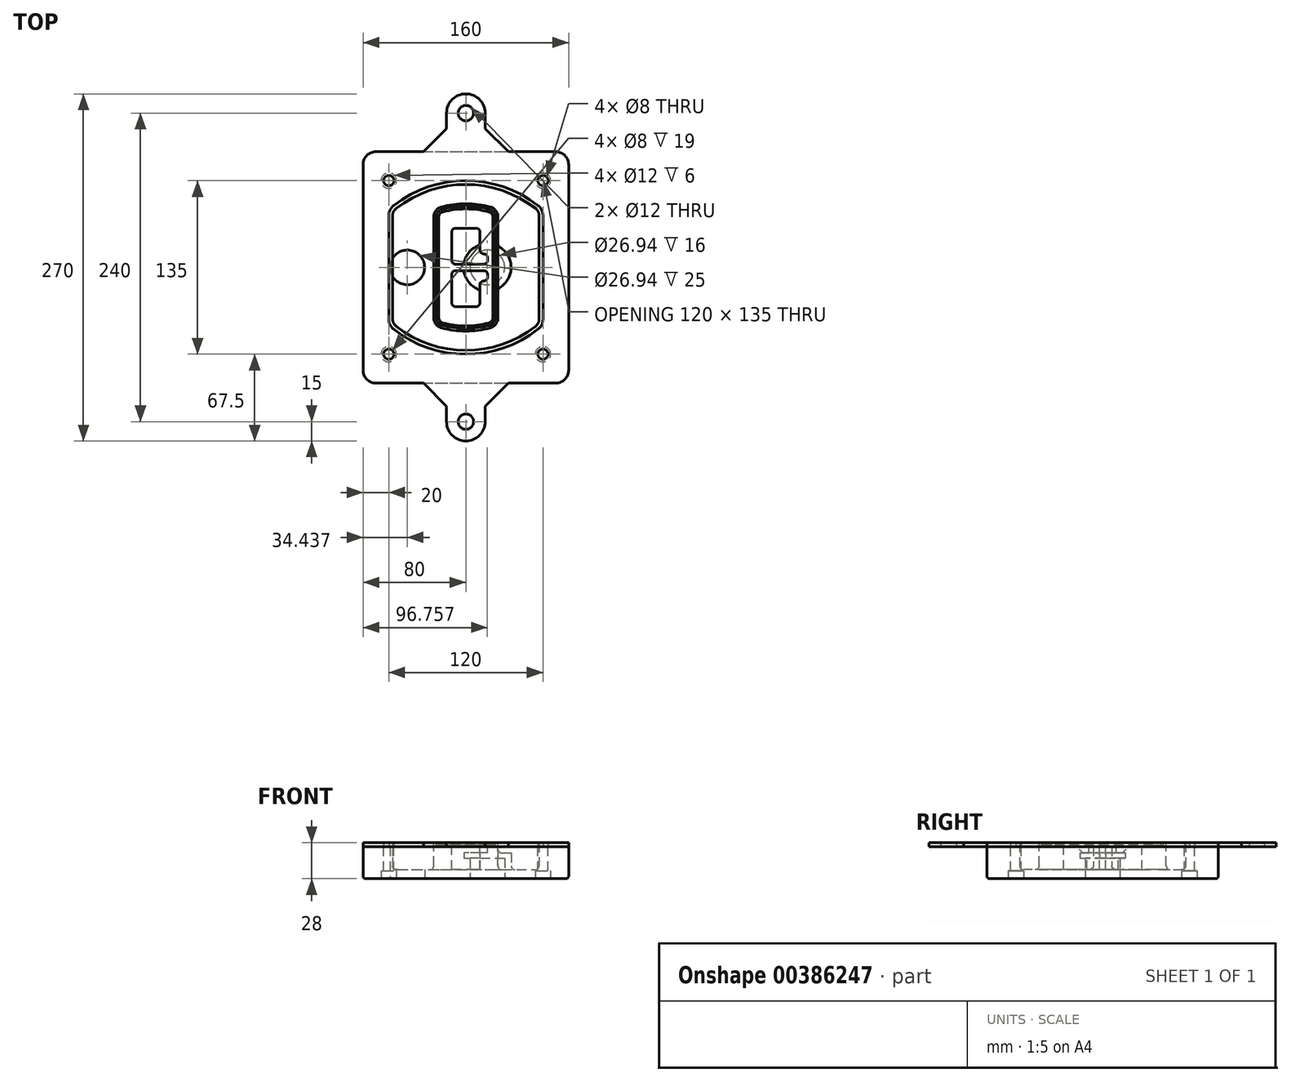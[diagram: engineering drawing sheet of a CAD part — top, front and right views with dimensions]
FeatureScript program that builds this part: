
annotation { "Feature Type Name" : "Feature", "Feature Type Description" : "" }
export const myFeature = defineFeature(function(context is Context, id is Id, definition is map)
    precondition{}
    {
        {
            var Q0;
            Q0=qCreatedBy(makeId("Top.planeOp"),FACE);
            var sketch = newSketch(context, id + "F0", { "sketchPlane" : qUnion([Q0])});
            skPoint(sketch, "E0.rect.middle", {"position": v(0, 0) * mm});
            skLineSegment(sketch, "E1.bottom", {"start": v(-70, -90) * mm, "end": v(70, -90) * mm});
            skLineSegment(sketch, "E1.top", {"start": v(-70, 90) * mm, "end": v(70, 90) * mm});
            skLineSegment(sketch, "E1.left", {"start": v(-80, -80) * mm, "end": v(-80, 80) * mm});
            skLineSegment(sketch, "E1.right", {"start": v(80, -80) * mm, "end": v(80, 80) * mm});
            skLineSegment(sketch, "E2", {"start": v(-80, 90) * mm, "end": v(80, -90) * mm, "construction": true});
            skLineSegment(sketch, "E3", {"start": v(80, 90) * mm, "end": v(-80, -90) * mm, "construction": true});
            skCircle(sketch, "E4", {"center": v(-60, 67.5) * mm, "radius": 4 * mm});
            skCircle(sketch, "E5", {"center": v(60, 67.5) * mm, "radius": 4 * mm});
            skCircle(sketch, "E6", {"center": v(60, -67.5) * mm, "radius": 4 * mm});
            skCircle(sketch, "E7", {"center": v(-60, -67.5) * mm, "radius": 4 * mm});
            skLineSegment(sketch, "E8", {"start": v(-60, 67.5) * mm, "end": v(60, 67.5) * mm, "construction": true});
            skLineSegment(sketch, "E9", {"start": v(60, 67.5) * mm, "end": v(60, -67.5) * mm, "construction": true});
            skLineSegment(sketch, "E10", {"start": v(60, -67.5) * mm, "end": v(-60, -67.5) * mm, "construction": true});
            skLineSegment(sketch, "E11", {"start": v(-60, -67.5) * mm, "end": v(-60, 67.5) * mm, "construction": true});
            skLineSegment(sketch, "E12", {"start": v(-60, 40.3) * mm, "end": v(-60, -40.3) * mm});
            skLineSegment(sketch, "E13", {"start": v(60, 40.3) * mm, "end": v(60, -40.3) * mm});
            skArc(sketch, "E14", {"start": v(56.15, 48.18) * mm, "mid": v(0, 67.5) * mm, "end": v(-56.15, 48.18) * mm});
            skArc(sketch, "E15", {"start": v(-56.15, -48.18) * mm, "mid": v(0, -67.5) * mm, "end": v(56.15, -48.18) * mm});
            skLineSegment(sketch, "E16", {"start": v(-60, 0) * mm, "end": v(60, 0) * mm, "construction": true});
            skPoint(sketch, "E17.visualSharp", {"position": v(-60, -45) * mm});
            skArc(sketch, "E17.filletArc", {"start": v(-60, -40.3) * mm, "mid": v(-58.99, -44.68) * mm, "end": v(-56.15, -48.18) * mm});
            skPoint(sketch, "E18.visualSharp", {"position": v(-60, 45) * mm});
            skArc(sketch, "E18.filletArc", {"start": v(-56.15, 48.18) * mm, "mid": v(-58.99, 44.68) * mm, "end": v(-60, 40.3) * mm});
            skPoint(sketch, "E19.visualSharp", {"position": v(60, 45) * mm});
            skArc(sketch, "E19.filletArc", {"start": v(60, 40.3) * mm, "mid": v(58.99, 44.68) * mm, "end": v(56.15, 48.18) * mm});
            skPoint(sketch, "E20.visualSharp", {"position": v(60, -45) * mm});
            skArc(sketch, "E20.filletArc", {"start": v(56.15, -48.18) * mm, "mid": v(58.99, -44.68) * mm, "end": v(60, -40.3) * mm});
            skPoint(sketch, "E21.visualSharp", {"position": v(-80, 90) * mm});
            skArc(sketch, "E21.filletArc", {"start": v(-70, 90) * mm, "mid": v(-77.07, 87.07) * mm, "end": v(-80, 80) * mm});
            skPoint(sketch, "E22.visualSharp", {"position": v(80, 90) * mm});
            skArc(sketch, "E22.filletArc", {"start": v(80, 80) * mm, "mid": v(77.07, 87.07) * mm, "end": v(70, 90) * mm});
            skPoint(sketch, "E23.visualSharp", {"position": v(80, -90) * mm});
            skArc(sketch, "E23.filletArc", {"start": v(70, -90) * mm, "mid": v(77.07, -87.07) * mm, "end": v(80, -80) * mm});
            skPoint(sketch, "E24.visualSharp", {"position": v(-80, -90) * mm});
            skArc(sketch, "E24.filletArc", {"start": v(-80, -80) * mm, "mid": v(-77.07, -87.07) * mm, "end": v(-70, -90) * mm});
            skArc(sketch, "E25.0", {"start": v(57, 40.3) * mm, "mid": v(56.3, 43.36) * mm, "end": v(54.3, 45.81) * mm});
            skLineSegment(sketch, "E25.1", {"start": v(57, 40.3) * mm, "end": v(57, -40.3) * mm});
            skArc(sketch, "E25.2", {"start": v(54.3, -45.81) * mm, "mid": v(56.3, -43.36) * mm, "end": v(57, -40.3) * mm});
            skArc(sketch, "E25.3", {"start": v(-54.3, -45.81) * mm, "mid": v(0, -64.5) * mm, "end": v(54.3, -45.81) * mm});
            skArc(sketch, "E25.4", {"start": v(-57, -40.3) * mm, "mid": v(-56.3, -43.36) * mm, "end": v(-54.3, -45.81) * mm});
            skArc(sketch, "E25.5", {"start": v(54.3, 45.81) * mm, "mid": v(0, 64.5) * mm, "end": v(-54.3, 45.81) * mm});
            skLineSegment(sketch, "E25.6", {"start": v(-57, 40.3) * mm, "end": v(-57, -40.3) * mm});
            skArc(sketch, "E25.7", {"start": v(-54.3, 45.81) * mm, "mid": v(-56.3, 43.36) * mm, "end": v(-57, 40.3) * mm});
            skArc(sketch, "E26.0", {"start": v(-58.62, 51.33) * mm, "mid": v(-62.58, 46.43) * mm, "end": v(-64, 40.3) * mm});
            skArc(sketch, "E26.1", {"start": v(58.62, 51.33) * mm, "mid": v(0, 71.5) * mm, "end": v(-58.62, 51.33) * mm});
            skArc(sketch, "E26.2", {"start": v(64, 40.3) * mm, "mid": v(62.58, 46.43) * mm, "end": v(58.62, 51.33) * mm});
            skLineSegment(sketch, "E26.3", {"start": v(64, 40.3) * mm, "end": v(64, -40.3) * mm});
            skArc(sketch, "E26.4", {"start": v(58.62, -51.33) * mm, "mid": v(62.58, -46.43) * mm, "end": v(64, -40.3) * mm});
            skLineSegment(sketch, "E26.5", {"start": v(-64, 40.3) * mm, "end": v(-64, -40.3) * mm});
            skArc(sketch, "E26.6", {"start": v(-58.62, -51.33) * mm, "mid": v(0, -71.5) * mm, "end": v(58.62, -51.33) * mm});
            skArc(sketch, "E26.7", {"start": v(-64, -40.3) * mm, "mid": v(-62.58, -46.43) * mm, "end": v(-58.62, -51.33) * mm});
            skSolve(sketch);
        }
        {
            var Q0;
            Q0=makeQuery(id+"F0.imprint","IMPRINT",FACE,{"disambiguationData":[TD([[makeQuery(id+"F0.imprint","IMPRINT",EDGE,{"derivedFrom":sQuery(id+"F0.wireOp",EDGE,"E1.bottom")}),1.0]])]});
            var Q1;
            Q1=makeQuery(id+"F0.imprint","IMPRINT",FACE,{"disambiguationData":[TD([[makeQuery(id+"F0.imprint","IMPRINT",EDGE,{"derivedFrom":sQuery(id+"F0.wireOp",EDGE,"E12")}),1.0]])]});
            var Q2;
            Q2=makeQuery(id+"F0.imprint","IMPRINT",FACE,{"disambiguationData":[TD([[makeQuery(id+"F0.imprint","IMPRINT",EDGE,{"derivedFrom":sQuery(id+"F0.wireOp",EDGE,"E25.0")}),1.0]])]});
            var Q3;
            Q3=makeQuery(id+"F0.imprint","IMPRINT",FACE,{"disambiguationData":[TD([[makeQuery(id+"F0.imprint","IMPRINT",EDGE,{"derivedFrom":sQuery(id+"F0.wireOp",EDGE,"E12")}),-1.0]])]});
            extrude(context, id + "F1", {"entities" : qUnion([Q0, Q1, Q2, Q3]), "oppositeDirection" : true, "depth" : 25 * mm});
        }
        {
            var Q0;
            Q0=makeQuery(id+"F0.imprint","IMPRINT",FACE,{"disambiguationData":[TD([[makeQuery(id+"F0.imprint","IMPRINT",EDGE,{"derivedFrom":sQuery(id+"F0.wireOp",EDGE,"E12")}),1.0]])]});
            extrude(context, id + "F2", {"entities" : qUnion([Q0]), "operationType" : NewBodyOperationType.ADD, "depth" : 3 * mm});
        }
        {
            var Q0;
            Q0=makeQuery(id+"F0.imprint","IMPRINT",FACE,{"disambiguationData":[TD([[makeQuery(id+"F0.imprint","IMPRINT",EDGE,{"derivedFrom":sQuery(id+"F0.wireOp",EDGE,"E25.0")}),1.0]])]});
            extrude(context, id + "F3", {"entities" : qUnion([Q0]), "operationType" : NewBodyOperationType.REMOVE, "oppositeDirection" : true, "depth" : 18 * mm});
        }
        {
            var Q0;
            Q0=makeQuery(id+"F2.opExtrude","CAP_FACE",FACE,{"disambiguationData":[OSD([sQuery(id+"F0.wireOp",EDGE,"E12"),sQuery(id+"F0.wireOp",EDGE,"E13"),sQuery(id+"F0.wireOp",EDGE,"E14"),sQuery(id+"F0.wireOp",EDGE,"E15"),sQuery(id+"F0.wireOp",EDGE,"E17.filletArc"),sQuery(id+"F0.wireOp",EDGE,"E18.filletArc"),sQuery(id+"F0.wireOp",EDGE,"E19.filletArc"),sQuery(id+"F0.wireOp",EDGE,"E20.filletArc"),sQuery(id+"F0.wireOp",EDGE,"E25.0"),sQuery(id+"F0.wireOp",EDGE,"E25.1"),sQuery(id+"F0.wireOp",EDGE,"E25.2"),sQuery(id+"F0.wireOp",EDGE,"E25.3"),sQuery(id+"F0.wireOp",EDGE,"E25.4"),sQuery(id+"F0.wireOp",EDGE,"E25.5"),sQuery(id+"F0.wireOp",EDGE,"E25.6"),sQuery(id+"F0.wireOp",EDGE,"E25.7")])],"isStart":false});
            var sketch = newSketch(context, id + "F4", { "sketchPlane" : qUnion([Q0])});
            skArc(sketch, "E27.0", {"start": v(-19.08, -46.97) * mm, "mid": v(0, -49.5) * mm, "end": v(19.08, -46.97) * mm});
            skArc(sketch, "E28.0", {"start": v(19.08, 46.97) * mm, "mid": v(0, 49.5) * mm, "end": v(-19.08, 46.97) * mm});
            skLineSegment(sketch, "E29", {"start": v(-25, 39.25) * mm, "end": v(-25, -39.25) * mm});
            skLineSegment(sketch, "E30", {"start": v(25, 39.25) * mm, "end": v(25, -39.25) * mm});
            skLineSegment(sketch, "E31", {"start": v(-25, 45.1) * mm, "end": v(25, 45.1) * mm, "construction": true});
            skLineSegment(sketch, "E32", {"start": v(-25, -45.1) * mm, "end": v(25, -45.1) * mm, "construction": true});
            skPoint(sketch, "E33.visualSharp", {"position": v(-25, 45.1) * mm});
            skArc(sketch, "E33.filletArc", {"start": v(-19.08, 46.97) * mm, "mid": v(-23.35, 44.11) * mm, "end": v(-25, 39.25) * mm});
            skPoint(sketch, "E34.visualSharp", {"position": v(25, 45.1) * mm});
            skArc(sketch, "E34.filletArc", {"start": v(25, 39.25) * mm, "mid": v(23.35, 44.11) * mm, "end": v(19.08, 46.97) * mm});
            skPoint(sketch, "E35.visualSharp", {"position": v(25, -45.1) * mm});
            skArc(sketch, "E35.filletArc", {"start": v(19.08, -46.97) * mm, "mid": v(23.35, -44.11) * mm, "end": v(25, -39.25) * mm});
            skPoint(sketch, "E36.visualSharp", {"position": v(-25, -45.1) * mm});
            skArc(sketch, "E36.filletArc", {"start": v(-25, -39.25) * mm, "mid": v(-23.35, -44.11) * mm, "end": v(-19.08, -46.97) * mm});
            skArc(sketch, "E37.0", {"start": v(54.3, 45.81) * mm, "mid": v(0, 64.5) * mm, "end": v(-54.3, 45.81) * mm});
            skArc(sketch, "E37.1", {"start": v(-54.3, 45.81) * mm, "mid": v(-56.3, 43.36) * mm, "end": v(-57, 40.3) * mm});
            skLineSegment(sketch, "E37.2", {"start": v(-57, 40.3) * mm, "end": v(-57, -40.3) * mm});
            skArc(sketch, "E37.3", {"start": v(-57, -40.3) * mm, "mid": v(-56.3, -43.36) * mm, "end": v(-54.3, -45.81) * mm});
            skArc(sketch, "E37.4", {"start": v(-54.3, -45.81) * mm, "mid": v(0, -64.5) * mm, "end": v(54.3, -45.81) * mm});
            skArc(sketch, "E37.5", {"start": v(54.3, -45.81) * mm, "mid": v(56.3, -43.36) * mm, "end": v(57, -40.3) * mm});
            skLineSegment(sketch, "E37.6", {"start": v(57, 40.3) * mm, "end": v(57, -40.3) * mm});
            skArc(sketch, "E37.7", {"start": v(57, 40.3) * mm, "mid": v(56.3, 43.36) * mm, "end": v(54.3, 45.81) * mm});
            skLineSegment(sketch, "E38.0", {"start": v(23, 39.25) * mm, "end": v(23, -39.25) * mm});
            skArc(sketch, "E38.1", {"start": v(18.56, -45.04) * mm, "mid": v(21.76, -42.9) * mm, "end": v(23, -39.25) * mm});
            skArc(sketch, "E38.2", {"start": v(-18.56, -45.04) * mm, "mid": v(0, -47.5) * mm, "end": v(18.56, -45.04) * mm});
            skArc(sketch, "E38.3", {"start": v(-23, -39.25) * mm, "mid": v(-21.76, -42.9) * mm, "end": v(-18.56, -45.04) * mm});
            skLineSegment(sketch, "E38.4", {"start": v(-23, 39.25) * mm, "end": v(-23, -39.25) * mm});
            skArc(sketch, "E38.5", {"start": v(23, 39.25) * mm, "mid": v(21.76, 42.9) * mm, "end": v(18.56, 45.04) * mm});
            skArc(sketch, "E38.6", {"start": v(-18.56, 45.04) * mm, "mid": v(-21.76, 42.9) * mm, "end": v(-23, 39.25) * mm});
            skArc(sketch, "E38.7", {"start": v(18.56, 45.04) * mm, "mid": v(0, 47.5) * mm, "end": v(-18.56, 45.04) * mm});
            skArc(sketch, "E39.0", {"start": v(21, 39.25) * mm, "mid": v(20.18, 41.68) * mm, "end": v(18.04, 43.1) * mm});
            skLineSegment(sketch, "E39.1", {"start": v(21, 39.25) * mm, "end": v(21, -39.25) * mm});
            skArc(sketch, "E39.2", {"start": v(18.04, -43.1) * mm, "mid": v(20.18, -41.68) * mm, "end": v(21, -39.25) * mm});
            skArc(sketch, "E39.3", {"start": v(-18.04, -43.1) * mm, "mid": v(0, -45.5) * mm, "end": v(18.04, -43.1) * mm});
            skArc(sketch, "E39.4", {"start": v(-21, -39.25) * mm, "mid": v(-20.18, -41.68) * mm, "end": v(-18.04, -43.1) * mm});
            skArc(sketch, "E39.5", {"start": v(18.04, 43.1) * mm, "mid": v(0, 45.5) * mm, "end": v(-18.04, 43.1) * mm});
            skLineSegment(sketch, "E39.6", {"start": v(-21, 39.25) * mm, "end": v(-21, -39.25) * mm});
            skArc(sketch, "E39.7", {"start": v(-18.04, 43.1) * mm, "mid": v(-20.18, 41.68) * mm, "end": v(-21, 39.25) * mm});
            skLineSegment(sketch, "E40", {"start": v(-25, 0) * mm, "end": v(25, 0) * mm, "construction": true});
            skLineSegment(sketch, "E41", {"start": v(-11, 5.5) * mm, "end": v(-11, 27.5) * mm});
            skLineSegment(sketch, "E42", {"start": v(-8, 30.5) * mm, "end": v(8, 30.5) * mm});
            skLineSegment(sketch, "E43", {"start": v(11, 27.5) * mm, "end": v(11, 13.5) * mm});
            skLineSegment(sketch, "E44", {"start": v(14, 10.5) * mm, "end": v(14, 10.5) * mm});
            skLineSegment(sketch, "E45", {"start": v(17, 7.5) * mm, "end": v(17, 5.5) * mm});
            skLineSegment(sketch, "E46", {"start": v(14, 2.5) * mm, "end": v(-8, 2.5) * mm});
            skPoint(sketch, "E47.visualSharp", {"position": v(-11, 30.5) * mm});
            skArc(sketch, "E47.filletArc", {"start": v(-8, 30.5) * mm, "mid": v(-10.12, 29.62) * mm, "end": v(-11, 27.5) * mm});
            skPoint(sketch, "E48.visualSharp", {"position": v(11, 30.5) * mm});
            skArc(sketch, "E48.filletArc", {"start": v(11, 27.5) * mm, "mid": v(10.12, 29.62) * mm, "end": v(8, 30.5) * mm});
            skPoint(sketch, "E49.visualSharp", {"position": v(11, 10.5) * mm});
            skArc(sketch, "E49.filletArc", {"start": v(11, 13.5) * mm, "mid": v(11.88, 11.38) * mm, "end": v(14, 10.5) * mm});
            skPoint(sketch, "E50.visualSharp", {"position": v(17, 10.5) * mm});
            skArc(sketch, "E50.filletArc", {"start": v(17, 7.5) * mm, "mid": v(16.12, 9.62) * mm, "end": v(14, 10.5) * mm});
            skPoint(sketch, "E51.visualSharp", {"position": v(17, 2.5) * mm});
            skArc(sketch, "E51.filletArc", {"start": v(14, 2.5) * mm, "mid": v(16.12, 3.38) * mm, "end": v(17, 5.5) * mm});
            skPoint(sketch, "E52.visualSharp", {"position": v(-11, 2.5) * mm});
            skArc(sketch, "E52.filletArc", {"start": v(-11, 5.5) * mm, "mid": v(-10.12, 3.38) * mm, "end": v(-8, 2.5) * mm});
            skLineSegment(sketch, "E53.0.MirrorCS", {"start": v(14, -2.5) * mm, "end": v(-8, -2.5) * mm});
            skArc(sketch, "E54.0.MirrorCS", {"start": v(-11, -5.5) * mm, "mid": v(-10.12, -3.38) * mm, "end": v(-8, -2.5) * mm});
            skLineSegment(sketch, "E55.0.MirrorCS", {"start": v(-11, -5.5) * mm, "end": v(-11, -27.5) * mm});
            skArc(sketch, "E56.0.MirrorCS", {"start": v(-8, -30.5) * mm, "mid": v(-10.12, -29.62) * mm, "end": v(-11, -27.5) * mm});
            skLineSegment(sketch, "E57.0.MirrorCS", {"start": v(-8, -30.5) * mm, "end": v(8, -30.5) * mm});
            skArc(sketch, "E58.0.MirrorCS", {"start": v(11, -27.5) * mm, "mid": v(10.12, -29.62) * mm, "end": v(8, -30.5) * mm});
            skLineSegment(sketch, "E59.0.MirrorCS", {"start": v(11, -27.5) * mm, "end": v(11, -13.5) * mm});
            skArc(sketch, "E60.0.MirrorCS", {"start": v(11, -13.5) * mm, "mid": v(11.88, -11.38) * mm, "end": v(14, -10.5) * mm});
            skArc(sketch, "E61.0.MirrorCS", {"start": v(17, -7.5) * mm, "mid": v(16.12, -9.62) * mm, "end": v(14, -10.5) * mm});
            skLineSegment(sketch, "E62.0.MirrorCS", {"start": v(17, -7.5) * mm, "end": v(17, -5.5) * mm});
            skArc(sketch, "E63.0.MirrorCS", {"start": v(14, -2.5) * mm, "mid": v(16.12, -3.38) * mm, "end": v(17, -5.5) * mm});
            skSolve(sketch);
        }
        {
            var Q0;
            Q0=makeQuery(id+"F4.imprint","IMPRINT",FACE,{"disambiguationData":[TD([[makeQuery(id+"F4.imprint","IMPRINT",EDGE,{"derivedFrom":sQuery(id+"F4.wireOp",EDGE,"E27.0")}),1.0]])]});
            var Q1;
            Q1=makeQuery(id+"F4.imprint","IMPRINT",FACE,{"disambiguationData":[TD([[makeQuery(id+"F4.imprint","IMPRINT",EDGE,{"derivedFrom":sQuery(id+"F4.wireOp",EDGE,"E38.0")}),-1.0]])]});
            var Q2;
            Q2=makeQuery(id+"F4.imprint","IMPRINT",FACE,{"disambiguationData":[TD([[makeQuery(id+"F4.imprint","IMPRINT",EDGE,{"derivedFrom":sQuery(id+"F4.wireOp",EDGE,"E39.0")}),1.0]])]});
            extrude(context, id + "F5", {"entities" : qUnion([Q0, Q1, Q2]), "operationType" : NewBodyOperationType.ADD, "endBound" : BoundingType.UP_TO_NEXT, "oppositeDirection" : true, "depth" : 25 * mm});
        }
        {
            var Q0;
            Q0=makeQuery(id+"F4.imprint","IMPRINT",FACE,{"disambiguationData":[TD([[makeQuery(id+"F4.imprint","IMPRINT",EDGE,{"derivedFrom":sQuery(id+"F4.wireOp",EDGE,"E38.0")}),-1.0]])]});
            extrude(context, id + "F6", {"entities" : qUnion([Q0]), "operationType" : NewBodyOperationType.REMOVE, "oppositeDirection" : true, "depth" : 2 * mm});
        }
        {
            var Q0;
            Q0=makeQuery(id+"F1.opExtrude","CAP_FACE",FACE,{"disambiguationData":[OSD([sQuery(id+"F0.wireOp",EDGE,"E1.bottom"),sQuery(id+"F0.wireOp",EDGE,"E1.top"),sQuery(id+"F0.wireOp",EDGE,"E1.left"),sQuery(id+"F0.wireOp",EDGE,"E1.right"),sQuery(id+"F0.wireOp",EDGE,"E4"),sQuery(id+"F0.wireOp",EDGE,"E5"),sQuery(id+"F0.wireOp",EDGE,"E6"),sQuery(id+"F0.wireOp",EDGE,"E7"),sQuery(id+"F0.wireOp",EDGE,"E21.filletArc"),sQuery(id+"F0.wireOp",EDGE,"E22.filletArc"),sQuery(id+"F0.wireOp",EDGE,"E23.filletArc"),sQuery(id+"F0.wireOp",EDGE,"E24.filletArc")])],"isStart":false});
            var sketch = newSketch(context, id + "F7", { "sketchPlane" : qUnion([Q0])});
            skCircle(sketch, "E64", {"center": v(16.76, 0) * mm, "radius": 13.47 * mm});
            skCircle(sketch, "E65", {"center": v(-45.56, 0) * mm, "radius": 13.47 * mm});
            skLineSegment(sketch, "E66", {"start": v(80, 0) * mm, "end": v(-80, 0) * mm});
            skCircle(sketch, "E67", {"center": v(16.76, 0) * mm, "radius": 18.47 * mm});
            skCircle(sketch, "E68", {"center": v(60, -67.5) * mm, "radius": 6 * mm});
            skCircle(sketch, "E69", {"center": v(-60, -67.5) * mm, "radius": 6 * mm});
            skCircle(sketch, "E70", {"center": v(-60, 67.5) * mm, "radius": 6 * mm});
            skCircle(sketch, "E71", {"center": v(60, 67.5) * mm, "radius": 6 * mm});
            skSolve(sketch);
        }
        {
            var Q0;
            {var subQ1=sQuery(id+"F7.wireOp",EDGE,"E66");var subQ4=sQuery(id+"F7.wireOp",EDGE,"E64");var subQ6=makeQuery(id+"F7.imprint","INTERSECT",VERTEX,{"disambiguationData":[OD(0.0)],"derivedFrom":[subQ4,subQ1]});Q0=makeQuery(id+"F7.imprint","IMPRINT",FACE,{"disambiguationData":[TD([[makeQuery(id+"F7.imprint","IMPRINT",EDGE,{"disambiguationData":[TD([[subQ6,-1.0]])],"derivedFrom":subQ4}),-1.0]])]});}
            var Q1;
            {var subQ0=sQuery(id+"F7.wireOp",EDGE,"E66");var subQ1=sQuery(id+"F7.wireOp",EDGE,"E64");var subQ3=makeQuery(id+"F7.imprint","INTERSECT",VERTEX,{"disambiguationData":[OD(0.0)],"derivedFrom":[subQ1,subQ0]});Q1=makeQuery(id+"F7.imprint","IMPRINT",FACE,{"disambiguationData":[TD([[makeQuery(id+"F7.imprint","IMPRINT",EDGE,{"disambiguationData":[TD([[subQ3,-1.0]])],"derivedFrom":subQ1}),1.0]])]});}
            var Q2;
            {var subQ0=sQuery(id+"F7.wireOp",EDGE,"E66");var subQ1=sQuery(id+"F7.wireOp",EDGE,"E64");var subQ3=makeQuery(id+"F7.imprint","INTERSECT",VERTEX,{"disambiguationData":[OD(0.0)],"derivedFrom":[subQ1,subQ0]});Q2=makeQuery(id+"F7.imprint","IMPRINT",FACE,{"disambiguationData":[TD([[makeQuery(id+"F7.imprint","IMPRINT",EDGE,{"disambiguationData":[TD([[subQ3,1.0]])],"derivedFrom":subQ1}),1.0]])]});}
            var Q3;
            {var subQ1=sQuery(id+"F7.wireOp",EDGE,"E66");var subQ4=sQuery(id+"F7.wireOp",EDGE,"E64");var subQ6=makeQuery(id+"F7.imprint","INTERSECT",VERTEX,{"disambiguationData":[OD(0.0)],"derivedFrom":[subQ4,subQ1]});Q3=makeQuery(id+"F7.imprint","IMPRINT",FACE,{"disambiguationData":[TD([[makeQuery(id+"F7.imprint","IMPRINT",EDGE,{"disambiguationData":[TD([[subQ6,1.0]])],"derivedFrom":subQ4}),-1.0]])]});}
            extrude(context, id + "F8", {"entities" : qUnion([Q0, Q1, Q2, Q3]), "operationType" : NewBodyOperationType.ADD, "oppositeDirection" : true, "depth" : 20 * mm});
        }
        {
            var Q0;
            {var subQ0=sQuery(id+"F7.wireOp",EDGE,"E66");var subQ1=sQuery(id+"F7.wireOp",EDGE,"E64");var subQ3=makeQuery(id+"F7.imprint","INTERSECT",VERTEX,{"disambiguationData":[OD(0.0)],"derivedFrom":[subQ1,subQ0]});Q0=makeQuery(id+"F7.imprint","IMPRINT",FACE,{"disambiguationData":[TD([[makeQuery(id+"F7.imprint","IMPRINT",EDGE,{"disambiguationData":[TD([[subQ3,-1.0]])],"derivedFrom":subQ1}),1.0]])]});}
            var Q1;
            {var subQ0=sQuery(id+"F7.wireOp",EDGE,"E66");var subQ1=sQuery(id+"F7.wireOp",EDGE,"E64");var subQ3=makeQuery(id+"F7.imprint","INTERSECT",VERTEX,{"disambiguationData":[OD(0.0)],"derivedFrom":[subQ1,subQ0]});Q1=makeQuery(id+"F7.imprint","IMPRINT",FACE,{"disambiguationData":[TD([[makeQuery(id+"F7.imprint","IMPRINT",EDGE,{"disambiguationData":[TD([[subQ3,1.0]])],"derivedFrom":subQ1}),1.0]])]});}
            extrude(context, id + "F9", {"entities" : qUnion([Q0, Q1]), "operationType" : NewBodyOperationType.REMOVE, "oppositeDirection" : true, "depth" : 16 * mm});
        }
        {
            var Q0;
            {var subQ0=sQuery(id+"F7.wireOp",EDGE,"E66");var subQ1=sQuery(id+"F7.wireOp",EDGE,"E65");var subQ3=makeQuery(id+"F7.imprint","INTERSECT",VERTEX,{"disambiguationData":[OD(0.0)],"derivedFrom":[subQ1,subQ0]});Q0=makeQuery(id+"F7.imprint","IMPRINT",FACE,{"disambiguationData":[TD([[makeQuery(id+"F7.imprint","IMPRINT",EDGE,{"disambiguationData":[TD([[subQ3,-1.0]])],"derivedFrom":subQ1}),1.0]])]});}
            var Q1;
            {var subQ0=sQuery(id+"F7.wireOp",EDGE,"E66");var subQ1=sQuery(id+"F7.wireOp",EDGE,"E65");var subQ3=makeQuery(id+"F7.imprint","INTERSECT",VERTEX,{"disambiguationData":[OD(0.0)],"derivedFrom":[subQ1,subQ0]});Q1=makeQuery(id+"F7.imprint","IMPRINT",FACE,{"disambiguationData":[TD([[makeQuery(id+"F7.imprint","IMPRINT",EDGE,{"disambiguationData":[TD([[subQ3,1.0]])],"derivedFrom":subQ1}),1.0]])]});}
            extrude(context, id + "F10", {"entities" : qUnion([Q0, Q1]), "operationType" : NewBodyOperationType.REMOVE, "oppositeDirection" : true, "depth" : 25 * mm});
        }
        {
            var Q0;
            Q0=makeQuery(id+"F7.imprint","IMPRINT",FACE,{"disambiguationData":[TD([[makeQuery(id+"F7.imprint","IMPRINT",EDGE,{"derivedFrom":sQuery(id+"F7.wireOp",EDGE,"E68")}),1.0]])]});
            var Q1;
            Q1=makeQuery(id+"F7.imprint","IMPRINT",FACE,{"disambiguationData":[TD([[makeQuery(id+"F7.imprint","IMPRINT",EDGE,{"derivedFrom":makeQuery(id+"F1.opExtrude","CAP_EDGE",EDGE,{"disambiguationData":[OSD([sQuery(id+"F0.wireOp",EDGE,"E5")])],"isStart":false})}),-1.0]])]});
            var Q2;
            Q2=makeQuery(id+"F7.imprint","IMPRINT",FACE,{"disambiguationData":[TD([[makeQuery(id+"F7.imprint","IMPRINT",EDGE,{"derivedFrom":sQuery(id+"F7.wireOp",EDGE,"E69")}),1.0]])]});
            var Q3;
            Q3=makeQuery(id+"F7.imprint","IMPRINT",FACE,{"disambiguationData":[TD([[makeQuery(id+"F7.imprint","IMPRINT",EDGE,{"derivedFrom":makeQuery(id+"F1.opExtrude","CAP_EDGE",EDGE,{"disambiguationData":[OSD([sQuery(id+"F0.wireOp",EDGE,"E4")])],"isStart":false})}),-1.0]])]});
            var Q4;
            Q4=makeQuery(id+"F7.imprint","IMPRINT",FACE,{"disambiguationData":[TD([[makeQuery(id+"F7.imprint","IMPRINT",EDGE,{"derivedFrom":sQuery(id+"F7.wireOp",EDGE,"E70")}),1.0]])]});
            var Q5;
            Q5=makeQuery(id+"F7.imprint","IMPRINT",FACE,{"disambiguationData":[TD([[makeQuery(id+"F7.imprint","IMPRINT",EDGE,{"derivedFrom":makeQuery(id+"F1.opExtrude","CAP_EDGE",EDGE,{"disambiguationData":[OSD([sQuery(id+"F0.wireOp",EDGE,"E7")])],"isStart":false})}),-1.0]])]});
            var Q6;
            Q6=makeQuery(id+"F7.imprint","IMPRINT",FACE,{"disambiguationData":[TD([[makeQuery(id+"F7.imprint","IMPRINT",EDGE,{"derivedFrom":sQuery(id+"F7.wireOp",EDGE,"E71")}),1.0]])]});
            var Q7;
            Q7=makeQuery(id+"F7.imprint","IMPRINT",FACE,{"disambiguationData":[TD([[makeQuery(id+"F7.imprint","IMPRINT",EDGE,{"derivedFrom":makeQuery(id+"F1.opExtrude","CAP_EDGE",EDGE,{"disambiguationData":[OSD([sQuery(id+"F0.wireOp",EDGE,"E6")])],"isStart":false})}),-1.0]])]});
            extrude(context, id + "F11", {"entities" : qUnion([Q0, Q1, Q2, Q3, Q4, Q5, Q6, Q7]), "operationType" : NewBodyOperationType.REMOVE, "oppositeDirection" : true, "depth" : 6 * mm});
        }
        {
            var Q0;
            Q0=makeQuery(id+"F9.boolean.opBoolean","COPY",FACE,{"derivedFrom":makeQuery(id+"F9.opExtrude","CAP_FACE",FACE,{"disambiguationData":[OSD([sQuery(id+"F7.wireOp",EDGE,"E64")])],"isStart":false})});
            var sketch = newSketch(context, id + "F12", { "sketchPlane" : qUnion([Q0])});
            skArc(sketch, "E72.0", {"start": v(11, 17.55) * mm, "mid": v(2.57, 11.82) * mm, "end": v(-1.54, 2.5) * mm});
            skArc(sketch, "E72.1", {"start": v(-1.54, -2.5) * mm, "mid": v(2.57, -11.82) * mm, "end": v(11, -17.55) * mm});
            skLineSegment(sketch, "E73", {"start": v(-1.54, -2.5) * mm, "end": v(14, -2.5) * mm});
            skLineSegment(sketch, "E74.0", {"start": v(14, 2.5) * mm, "end": v(-1.54, 2.5) * mm});
            skArc(sketch, "E74.1", {"start": v(14, 2.5) * mm, "mid": v(16.12, 3.38) * mm, "end": v(17, 5.5) * mm});
            skLineSegment(sketch, "E74.2", {"start": v(17, 7.5) * mm, "end": v(17, 5.5) * mm});
            skArc(sketch, "E74.3", {"start": v(17, 7.5) * mm, "mid": v(16.12, 9.62) * mm, "end": v(14, 10.5) * mm});
            skArc(sketch, "E74.4", {"start": v(11, 13.5) * mm, "mid": v(11.88, 11.38) * mm, "end": v(14, 10.5) * mm});
            skLineSegment(sketch, "E74.5", {"start": v(11, 17.55) * mm, "end": v(11, 13.5) * mm});
            skLineSegment(sketch, "E74.7", {"start": v(14, -2.5) * mm, "end": v(-1.54, -2.5) * mm});
            skArc(sketch, "E74.8", {"start": v(14, -2.5) * mm, "mid": v(16.12, -3.38) * mm, "end": v(17, -5.5) * mm});
            skLineSegment(sketch, "E74.9", {"start": v(17, -7.5) * mm, "end": v(17, -5.5) * mm});
            skArc(sketch, "E74.10", {"start": v(17, -7.5) * mm, "mid": v(16.12, -9.62) * mm, "end": v(14, -10.5) * mm});
            skArc(sketch, "E74.11", {"start": v(11, -13.5) * mm, "mid": v(11.88, -11.38) * mm, "end": v(14, -10.5) * mm});
            skLineSegment(sketch, "E74.12", {"start": v(11, -17.55) * mm, "end": v(11, -13.5) * mm});
            skPoint(sketch, "E75.orphan", {"position": v(11, -27.5) * mm});
            skPoint(sketch, "E76.orphan", {"position": v(-8, -2.5) * mm});
            skPoint(sketch, "E77.orphan", {"position": v(-8, 2.5) * mm});
            skPoint(sketch, "E78.orphan", {"position": v(11, 27.5) * mm});
            skSolve(sketch);
        }
        {
            var Q0;
            {var subQ7=sQuery(id+"F12.wireOp",EDGE,"E72.0");var subQ14=sQuery(id+"F12.wireOp",EDGE,"E72.1");var subQ16=sQuery(id+"F12.wireOp",EDGE,"E74.1");var subQ18=sQuery(id+"F12.wireOp",EDGE,"E74.8");Q0=qUnion([makeQuery(id+"F12.imprint","IMPRINT",FACE,{"disambiguationData":[TD([[makeQuery(id+"F12.imprint","IMPRINT",EDGE,{"derivedFrom":subQ7}),1.0]])]}),makeQuery(id+"F12.imprint","IMPRINT",FACE,{"disambiguationData":[TD([[makeQuery(id+"F12.imprint","IMPRINT",EDGE,{"derivedFrom":subQ14}),1.0]])]}),makeQuery(id+"F12.imprint","IMPRINT",FACE,{"disambiguationData":[TD([[makeQuery(id+"F12.imprint","IMPRINT",EDGE,{"derivedFrom":subQ16}),1.0]])]}),makeQuery(id+"F12.imprint","IMPRINT",FACE,{"disambiguationData":[TD([[makeQuery(id+"F12.imprint","IMPRINT",EDGE,{"derivedFrom":subQ18}),-1.0]])]})]);}
            var Q1;
            Q1=makeQuery(id+"F5.boolean.opBoolean","SPLIT",FACE,{"disambiguationData":[TD([makeQuery(id+"F5.opExtrude","SWEPT_FACE",FACE,{"disambiguationData":[OSD([sQuery(id+"F4.wireOp",EDGE,"E41")])]})])],"derivedFrom":makeQuery(id+"F3.boolean.opBoolean","COPY",FACE,{"derivedFrom":makeQuery(id+"F3.opExtrude","CAP_FACE",FACE,{"disambiguationData":[OSD([sQuery(id+"F0.wireOp",EDGE,"E25.0"),sQuery(id+"F0.wireOp",EDGE,"E25.1"),sQuery(id+"F0.wireOp",EDGE,"E25.2"),sQuery(id+"F0.wireOp",EDGE,"E25.3"),sQuery(id+"F0.wireOp",EDGE,"E25.4"),sQuery(id+"F0.wireOp",EDGE,"E25.5"),sQuery(id+"F0.wireOp",EDGE,"E25.6"),sQuery(id+"F0.wireOp",EDGE,"E25.7")])],"isStart":false})})});
            extrude(context, id + "F13", {"entities" : qUnion([Q0]), "operationType" : NewBodyOperationType.REMOVE, "endBound" : BoundingType.UP_TO_SURFACE, "endBoundEntityFace" : qUnion([Q1]), "depth" : 25 * mm});
        }
        {
            var Q0;
            Q0=makeQuery(id+"F3.boolean.opBoolean","COPY",EDGE,{"derivedFrom":makeQuery(id+"F3.opExtrude","CAP_EDGE",EDGE,{"disambiguationData":[OSD([sQuery(id+"F0.wireOp",EDGE,"E25.6")])],"isStart":false})});
            var Q1;
            Q1=makeQuery(id+"F8.boolean.opBoolean","INTERSECT",EDGE,{"derivedFrom":[makeQuery(id+"F5.opExtrude","SWEPT_FACE",FACE,{"disambiguationData":[OSD([sQuery(id+"F4.wireOp",EDGE,"E30")])]}),makeQuery(id+"F8.opExtrude","CAP_FACE",FACE,{"disambiguationData":[OSD([sQuery(id+"F7.wireOp",EDGE,"E67")])],"isStart":false})]});
            var Q2;
            Q2=makeQuery(id+"F8.boolean.opBoolean","INTERSECT",EDGE,{"disambiguationData":[OD(1.0)],"derivedFrom":[makeQuery(id+"F5.opExtrude","SWEPT_FACE",FACE,{"disambiguationData":[OSD([sQuery(id+"F4.wireOp",EDGE,"E30")])]}),makeQuery(id+"F8.opExtrude","SWEPT_FACE",FACE,{"disambiguationData":[OSD([sQuery(id+"F7.wireOp",EDGE,"E67")])]})]});
            var Q3;
            {var subQ0=sQuery(id+"F4.wireOp",EDGE,"E30");Q3=makeQuery(id+"F8.boolean.opBoolean","SPLIT",EDGE,{"disambiguationData":[TD([makeQuery(id+"F5.opExtrude","SWEPT_FACE",FACE,{"disambiguationData":[OSD([sQuery(id+"F4.wireOp",EDGE,"E35.filletArc")])]})])],"derivedFrom":makeQuery(id+"F5.opExtrude","CAP_EDGE",EDGE,{"disambiguationData":[OSD([subQ0])],"isStart":false})});}
            var Q4;
            {var subQ0=sQuery(id+"F0.wireOp",EDGE,"E25.7");var subQ1=sQuery(id+"F0.wireOp",EDGE,"E25.1");var subQ2=sQuery(id+"F0.wireOp",EDGE,"E25.6");var subQ3=sQuery(id+"F0.wireOp",EDGE,"E25.5");var subQ4=sQuery(id+"F0.wireOp",EDGE,"E25.4");var subQ5=sQuery(id+"F0.wireOp",EDGE,"E25.0");var subQ6=sQuery(id+"F0.wireOp",EDGE,"E25.2");var subQ7=sQuery(id+"F0.wireOp",EDGE,"E25.3");Q4=makeQuery(id+"F8.boolean.opBoolean","INTERSECT",EDGE,{"derivedFrom":[makeQuery(id+"F5.boolean.opBoolean","SPLIT",FACE,{"disambiguationData":[TD([makeQuery(id+"F2.opExtrude","SWEPT_FACE",FACE,{"disambiguationData":[OSD([subQ5])]})])],"derivedFrom":makeQuery(id+"F3.boolean.opBoolean","COPY",FACE,{"derivedFrom":makeQuery(id+"F3.opExtrude","CAP_FACE",FACE,{"disambiguationData":[OSD([subQ5,subQ1,subQ6,subQ7,subQ4,subQ3,subQ2,subQ0])],"isStart":false})})}),makeQuery(id+"F8.opExtrude","SWEPT_FACE",FACE,{"disambiguationData":[OSD([sQuery(id+"F7.wireOp",EDGE,"E67")])]})]});}
            var Q5;
            Q5=makeQuery(id+"F8.boolean.opBoolean","INTERSECT",EDGE,{"disambiguationData":[OD(0.0)],"derivedFrom":[makeQuery(id+"F5.opExtrude","SWEPT_FACE",FACE,{"disambiguationData":[OSD([sQuery(id+"F4.wireOp",EDGE,"E30")])]}),makeQuery(id+"F8.opExtrude","SWEPT_FACE",FACE,{"disambiguationData":[OSD([sQuery(id+"F7.wireOp",EDGE,"E67")])]})]});
            fillet(context, id + "F14", {"entities" : qUnion([Q0, Q1, Q2, Q3, Q4, Q5]), "radius" : 3 * mm, "tangentPropagation" : true, "allowEdgeOverflow" : false});
        }
        {
            var Q0;
            Q0=makeQuery(id+"F1.opExtrude","CAP_EDGE",EDGE,{"disambiguationData":[OSD([sQuery(id+"F0.wireOp",EDGE,"E1.bottom")])],"isStart":false});
            fillet(context, id + "F15", {"entities" : qUnion([Q0]), "radius" : 2 * mm, "tangentPropagation" : true, "allowEdgeOverflow" : false});
        }
        {
            var Q0;
            {var subQ0=sQuery(id+"F0.wireOp",EDGE,"E21.filletArc");var subQ1=sQuery(id+"F0.wireOp",EDGE,"E7");var subQ2=sQuery(id+"F0.wireOp",EDGE,"E6");var subQ3=sQuery(id+"F0.wireOp",EDGE,"E5");var subQ4=sQuery(id+"F0.wireOp",EDGE,"E4");var subQ5=sQuery(id+"F0.wireOp",EDGE,"E22.filletArc");var subQ6=sQuery(id+"F0.wireOp",EDGE,"E1.bottom");var subQ7=sQuery(id+"F0.wireOp",EDGE,"E1.right");var subQ8=sQuery(id+"F0.wireOp",EDGE,"E1.top");var subQ9=sQuery(id+"F0.wireOp",EDGE,"E1.left");var subQ10=sQuery(id+"F0.wireOp",EDGE,"E23.filletArc");var subQ11=sQuery(id+"F0.wireOp",EDGE,"E24.filletArc");Q0=makeQuery(id+"F2.boolean.opBoolean","SPLIT",FACE,{"disambiguationData":[TD([makeQuery(id+"F1.opExtrude","SWEPT_FACE",FACE,{"disambiguationData":[OSD([subQ6])]})])],"derivedFrom":makeQuery(id+"F1.opExtrude","CAP_FACE",FACE,{"disambiguationData":[OSD([subQ6,subQ8,subQ9,subQ7,subQ4,subQ3,subQ2,subQ1,subQ0,subQ5,subQ10,subQ11])],"isStart":true})});}
            var sketch = newSketch(context, id + "F16", { "sketchPlane" : qUnion([Q0])});
            skLineSegment(sketch, "E79", {"start": v(0, 90) * mm, "end": v(0, 120) * mm, "construction": true});
            skPoint(sketch, "E79.endSnap0", {"position": v(0, 74.25) * mm});
            skCircle(sketch, "E80", {"center": v(0, 120) * mm, "radius": 6 * mm});
            skArc(sketch, "E81", {"start": v(15, 120) * mm, "mid": v(0, 135) * mm, "end": v(-15, 120) * mm});
            skLineSegment(sketch, "E82", {"start": v(-15, 120) * mm, "end": v(-15, 108) * mm});
            skLineSegment(sketch, "E83", {"start": v(-15, 108) * mm, "end": v(-33, 90) * mm});
            skLineSegment(sketch, "E84", {"start": v(15, 120) * mm, "end": v(15, 108) * mm});
            skLineSegment(sketch, "E85", {"start": v(15, 108) * mm, "end": v(33, 90) * mm});
            skLineSegment(sketch, "E86", {"start": v(-33, 90) * mm, "end": v(33, 90) * mm});
            skLineSegment(sketch, "E87", {"start": v(-80, 0) * mm, "end": v(80, 0) * mm, "construction": true});
            skPoint(sketch, "E88.MirrorP", {"position": v(0, -74.25) * mm});
            skLineSegment(sketch, "E89.MirrorCS", {"start": v(0, -90) * mm, "end": v(0, -120) * mm, "construction": true});
            skCircle(sketch, "E90.MirrorC", {"center": v(0, -120) * mm, "radius": 6 * mm});
            skLineSegment(sketch, "E91.MirrorCS", {"start": v(-15, -120) * mm, "end": v(-15, -108) * mm});
            skArc(sketch, "E92.MirrorCS", {"start": v(15, -120) * mm, "mid": v(0, -135) * mm, "end": v(-15, -120) * mm});
            skLineSegment(sketch, "E93.MirrorCS", {"start": v(-15, -108) * mm, "end": v(-33, -90) * mm});
            skLineSegment(sketch, "E94.MirrorCS", {"start": v(15, -120) * mm, "end": v(15, -108) * mm});
            skLineSegment(sketch, "E95.MirrorCS", {"start": v(15, -108) * mm, "end": v(33, -90) * mm});
            skLineSegment(sketch, "E96.MirrorCS", {"start": v(-33, -90) * mm, "end": v(33, -90) * mm});
            skSolve(sketch);
        }
        {
            var Q0;
            Q0 = qSketchRegion(id + "F16", true);
            var Q1;
            {var subQ4=sQuery(id+"F16.wireOp",EDGE,"E86");Q1=makeQuery(id+"F16.imprint","IMPRINT",FACE,{"disambiguationData":[TD([[makeQuery(id+"F16.imprint","IMPRINT",EDGE,{"derivedFrom":subQ4}),-1.0]])]});}
            var Q2;
            Q2=makeQuery(id+"F2.opExtrude","CAP_FACE",FACE,{"disambiguationData":[OSD([sQuery(id+"F0.wireOp",EDGE,"E12"),sQuery(id+"F0.wireOp",EDGE,"E13"),sQuery(id+"F0.wireOp",EDGE,"E14"),sQuery(id+"F0.wireOp",EDGE,"E15"),sQuery(id+"F0.wireOp",EDGE,"E17.filletArc"),sQuery(id+"F0.wireOp",EDGE,"E18.filletArc"),sQuery(id+"F0.wireOp",EDGE,"E19.filletArc"),sQuery(id+"F0.wireOp",EDGE,"E20.filletArc"),sQuery(id+"F0.wireOp",EDGE,"E25.0"),sQuery(id+"F0.wireOp",EDGE,"E25.1"),sQuery(id+"F0.wireOp",EDGE,"E25.2"),sQuery(id+"F0.wireOp",EDGE,"E25.3"),sQuery(id+"F0.wireOp",EDGE,"E25.4"),sQuery(id+"F0.wireOp",EDGE,"E25.5"),sQuery(id+"F0.wireOp",EDGE,"E25.6"),sQuery(id+"F0.wireOp",EDGE,"E25.7")])],"isStart":false});
            extrude(context, id + "F17", {"entities" : qUnion([Q0, Q1]), "endBound" : BoundingType.UP_TO_SURFACE, "endBoundEntityFace" : qUnion([Q2]), "depth" : 25 * mm});
        }
    });
